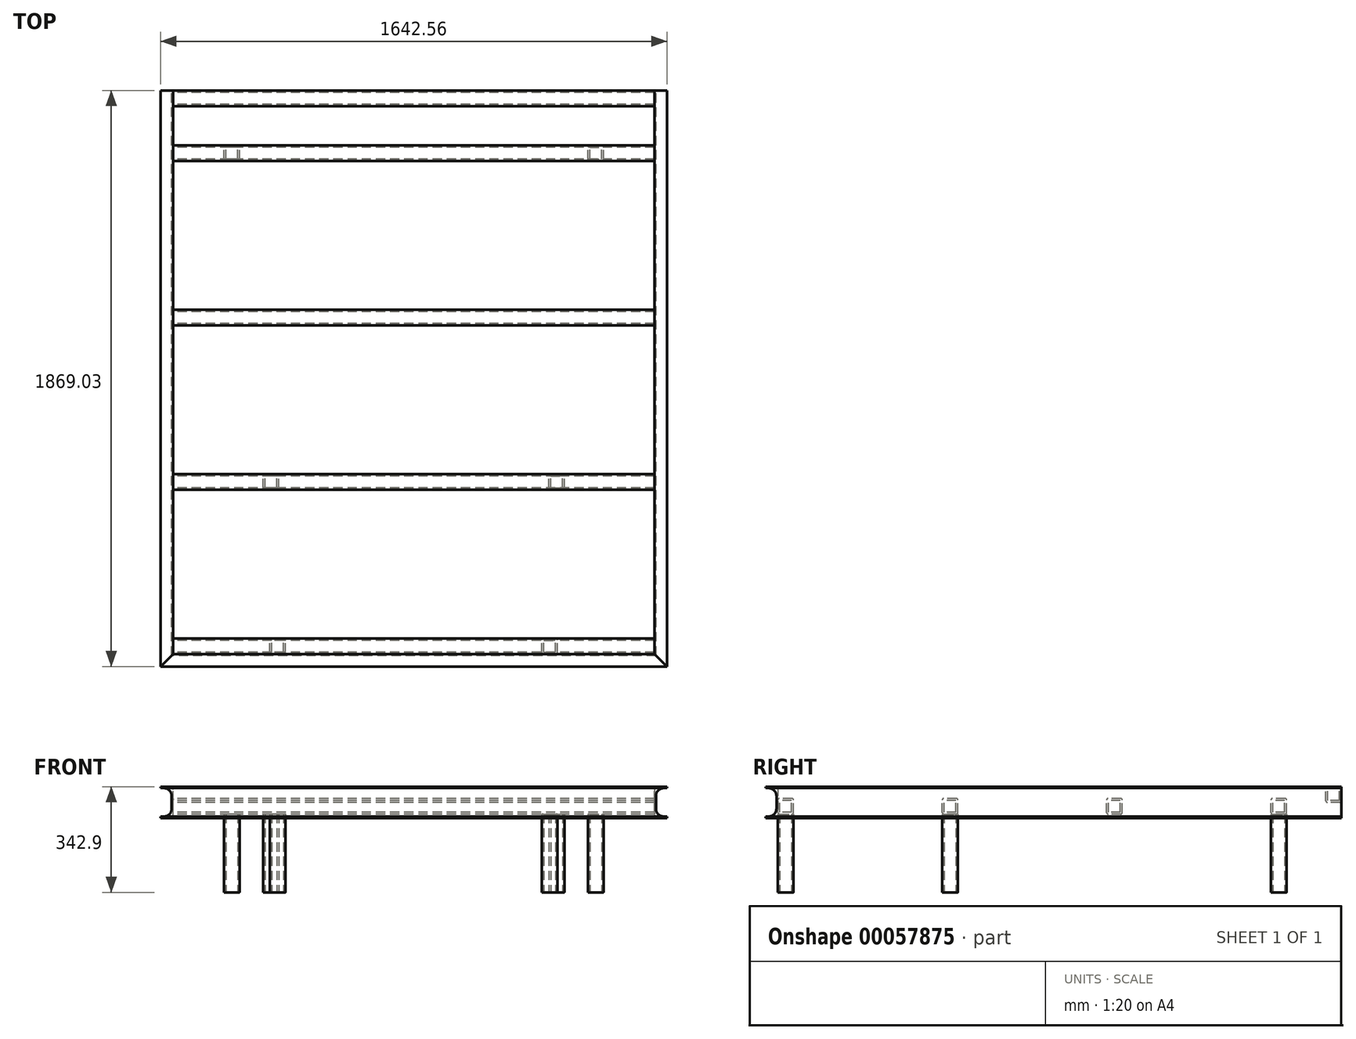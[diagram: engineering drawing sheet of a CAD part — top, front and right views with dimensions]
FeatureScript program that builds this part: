
annotation { "Feature Type Name" : "Feature", "Feature Type Description" : "" }
export const myFeature = defineFeature(function(context is Context, id is Id, definition is map)
    precondition{}
    {
        {
            var Q0;
            Q0=qCreatedBy(makeId("Top.planeOp"),FACE);
            var sketch = newSketch(context, id + "F0", { "sketchPlane" : qUnion([Q0])});
            skLineSegment(sketch, "E0.rect.bottom", {"start": v(-565.15, -25.4) * mm, "end": v(-615.95, -25.4) * mm});
            skLineSegment(sketch, "E0.rect.top", {"start": v(-565.15, 25.4) * mm, "end": v(-615.95, 25.4) * mm});
            skLineSegment(sketch, "E0.rect.left", {"start": v(-565.15, -25.4) * mm, "end": v(-565.15, 25.4) * mm});
            skLineSegment(sketch, "E0.rect.right", {"start": v(-615.95, -25.4) * mm, "end": v(-615.95, 25.4) * mm});
            skPoint(sketch, "E0.rect.middle", {"position": v(-590.55, 0) * mm});
            skLineSegment(sketch, "E1.rect.bottom", {"start": v(-571.5, -19.05) * mm, "end": v(-609.6, -19.05) * mm});
            skLineSegment(sketch, "E1.rect.top", {"start": v(-571.5, 19.05) * mm, "end": v(-609.6, 19.05) * mm});
            skLineSegment(sketch, "E1.rect.left", {"start": v(-571.5, -19.05) * mm, "end": v(-571.5, 19.05) * mm});
            skLineSegment(sketch, "E1.rect.right", {"start": v(-609.6, -19.05) * mm, "end": v(-609.6, 19.05) * mm});
            skLineSegment(sketch, "E2.rect.bottom", {"start": v(-438.15, -1092.2) * mm, "end": v(-488.95, -1092.2) * mm});
            skLineSegment(sketch, "E2.rect.top", {"start": v(-438.15, -1041.4) * mm, "end": v(-488.95, -1041.4) * mm});
            skLineSegment(sketch, "E2.rect.left", {"start": v(-438.15, -1092.2) * mm, "end": v(-438.15, -1041.4) * mm});
            skLineSegment(sketch, "E2.rect.right", {"start": v(-488.95, -1092.2) * mm, "end": v(-488.95, -1041.4) * mm});
            skPoint(sketch, "E2.rect.middle", {"position": v(-463.55, -1066.8) * mm});
            skLineSegment(sketch, "E3.rect.bottom", {"start": v(-444.5, -1085.85) * mm, "end": v(-482.6, -1085.85) * mm});
            skLineSegment(sketch, "E3.rect.top", {"start": v(-444.5, -1047.75) * mm, "end": v(-482.6, -1047.75) * mm});
            skLineSegment(sketch, "E3.rect.left", {"start": v(-444.5, -1085.85) * mm, "end": v(-444.5, -1047.75) * mm});
            skLineSegment(sketch, "E3.rect.right", {"start": v(-482.6, -1085.85) * mm, "end": v(-482.6, -1047.75) * mm});
            skLineSegment(sketch, "E4.rect.bottom", {"start": v(-415.93, -1625.6) * mm, "end": v(-466.73, -1625.6) * mm});
            skLineSegment(sketch, "E4.rect.top", {"start": v(-415.93, -1574.8) * mm, "end": v(-466.73, -1574.8) * mm});
            skLineSegment(sketch, "E4.rect.left", {"start": v(-415.93, -1625.6) * mm, "end": v(-415.93, -1574.8) * mm});
            skLineSegment(sketch, "E4.rect.right", {"start": v(-466.73, -1625.6) * mm, "end": v(-466.73, -1574.8) * mm});
            skPoint(sketch, "E4.rect.middle", {"position": v(-441.33, -1600.2) * mm});
            skLineSegment(sketch, "E5.rect.bottom", {"start": v(-422.28, -1619.25) * mm, "end": v(-460.38, -1619.25) * mm});
            skLineSegment(sketch, "E5.rect.top", {"start": v(-422.28, -1581.15) * mm, "end": v(-460.38, -1581.15) * mm});
            skLineSegment(sketch, "E5.rect.left", {"start": v(-422.28, -1619.25) * mm, "end": v(-422.28, -1581.15) * mm});
            skLineSegment(sketch, "E5.rect.right", {"start": v(-460.38, -1619.25) * mm, "end": v(-460.38, -1581.15) * mm});
            skLineSegment(sketch, "E6.MirrorCS", {"start": v(422.28, -1619.25) * mm, "end": v(460.38, -1619.25) * mm});
            skLineSegment(sketch, "E7.MirrorCS", {"start": v(565.15, -25.4) * mm, "end": v(615.95, -25.4) * mm});
            skLineSegment(sketch, "E8.MirrorCS", {"start": v(466.72, -1625.6) * mm, "end": v(466.72, -1574.8) * mm});
            skLineSegment(sketch, "E9.MirrorCS", {"start": v(422.28, -1581.15) * mm, "end": v(460.38, -1581.15) * mm});
            skLineSegment(sketch, "E10.MirrorCS", {"start": v(571.5, -19.05) * mm, "end": v(571.5, 19.05) * mm});
            skLineSegment(sketch, "E11.MirrorCS", {"start": v(571.5, 19.05) * mm, "end": v(609.6, 19.05) * mm});
            skLineSegment(sketch, "E12.MirrorCS", {"start": v(460.37, -1619.25) * mm, "end": v(460.37, -1581.15) * mm});
            skLineSegment(sketch, "E13.MirrorCS", {"start": v(571.5, -19.05) * mm, "end": v(609.6, -19.05) * mm});
            skLineSegment(sketch, "E14.MirrorCS", {"start": v(415.93, -1625.6) * mm, "end": v(466.73, -1625.6) * mm});
            skLineSegment(sketch, "E15.MirrorCS", {"start": v(565.15, -25.4) * mm, "end": v(565.15, 25.4) * mm});
            skLineSegment(sketch, "E16.MirrorCS", {"start": v(444.5, -1047.75) * mm, "end": v(482.6, -1047.75) * mm});
            skLineSegment(sketch, "E17.MirrorCS", {"start": v(422.27, -1619.25) * mm, "end": v(422.27, -1581.15) * mm});
            skLineSegment(sketch, "E18.MirrorCS", {"start": v(488.95, -1092.2) * mm, "end": v(488.95, -1041.4) * mm});
            skLineSegment(sketch, "E19.MirrorCS", {"start": v(609.6, -19.05) * mm, "end": v(609.6, 19.05) * mm});
            skLineSegment(sketch, "E20.MirrorCS", {"start": v(438.15, -1092.2) * mm, "end": v(488.95, -1092.2) * mm});
            skLineSegment(sketch, "E21.MirrorCS", {"start": v(415.93, -1574.8) * mm, "end": v(466.73, -1574.8) * mm});
            skLineSegment(sketch, "E22.MirrorCS", {"start": v(415.92, -1625.6) * mm, "end": v(415.92, -1574.8) * mm});
            skLineSegment(sketch, "E23.MirrorCS", {"start": v(482.6, -1085.85) * mm, "end": v(482.6, -1047.75) * mm});
            skLineSegment(sketch, "E24.MirrorCS", {"start": v(438.15, -1041.4) * mm, "end": v(488.95, -1041.4) * mm});
            skLineSegment(sketch, "E25.MirrorCS", {"start": v(615.95, -25.4) * mm, "end": v(615.95, 25.4) * mm});
            skLineSegment(sketch, "E26.MirrorCS", {"start": v(444.5, -1085.85) * mm, "end": v(482.6, -1085.85) * mm});
            skLineSegment(sketch, "E27.MirrorCS", {"start": v(438.15, -1092.2) * mm, "end": v(438.15, -1041.4) * mm});
            skLineSegment(sketch, "E28.MirrorCS", {"start": v(444.5, -1085.85) * mm, "end": v(444.5, -1047.75) * mm});
            skLineSegment(sketch, "E29.MirrorCS", {"start": v(565.15, 25.4) * mm, "end": v(615.95, 25.4) * mm});
            skPoint(sketch, "E30.MirrorP", {"position": v(441.33, -1600.2) * mm});
            skPoint(sketch, "E31.MirrorP", {"position": v(463.55, -1066.8) * mm});
            skPoint(sketch, "E32.MirrorP", {"position": v(590.55, 0) * mm});
            skSolve(sketch);
        }
        {
            var Q0;
            Q0 = qSketchRegion(id + "F0", true);
            extrude(context, id + "F1", {"entities" : qUnion([Q0]), "depth" : 254 * mm});
        }
        {
            var Q0;
            Q0=qCreatedBy(makeId("Right.planeOp"),FACE);
            var sketch = newSketch(context, id + "F2", { "sketchPlane" : qUnion([Q0])});
            skLineSegment(sketch, "E33.rect.bottom", {"start": v(25.4, 254) * mm, "end": v(-25.4, 254) * mm});
            skLineSegment(sketch, "E33.rect.top", {"start": v(25.4, 304.8) * mm, "end": v(-25.4, 304.8) * mm});
            skLineSegment(sketch, "E33.rect.left", {"start": v(25.4, 254) * mm, "end": v(25.4, 304.8) * mm});
            skLineSegment(sketch, "E33.rect.right", {"start": v(-25.4, 254) * mm, "end": v(-25.4, 304.8) * mm});
            skPoint(sketch, "E33.rect.middle", {"position": v(0, 279.4) * mm});
            skLineSegment(sketch, "E34.rect.bottom", {"start": v(19.05, 260.35) * mm, "end": v(-19.05, 260.35) * mm});
            skLineSegment(sketch, "E34.rect.top", {"start": v(19.05, 298.45) * mm, "end": v(-19.05, 298.45) * mm});
            skLineSegment(sketch, "E34.rect.left", {"start": v(19.05, 260.35) * mm, "end": v(19.05, 298.45) * mm});
            skLineSegment(sketch, "E34.rect.right", {"start": v(-19.05, 260.35) * mm, "end": v(-19.05, 298.45) * mm});
            skSolve(sketch);
        }
        {
            var Q0;
            Q0=makeQuery(id+"F2.imprint","IMPRINT",FACE,{"disambiguationData":[TD([[makeQuery(id+"F2.imprint","IMPRINT",EDGE,{"derivedFrom":sQuery(id+"F2.wireOp",EDGE,"E33.rect.bottom")}),-1.0]])]});
            extrude(context, id + "F3", {"entities" : qUnion([Q0]), "endBound" : BoundingType.SYMMETRIC, "depth" : 1562.1 * mm});
        }
        {
            var Q0;
            Q0=qCreatedBy(makeId("Right.planeOp"),FACE);
            var sketch = newSketch(context, id + "F4", { "sketchPlane" : qUnion([Q0])});
            skLineSegment(sketch, "E35.rect.bottom", {"start": v(-1041.4, 254) * mm, "end": v(-1092.2, 254) * mm});
            skLineSegment(sketch, "E35.rect.top", {"start": v(-1041.4, 304.8) * mm, "end": v(-1092.2, 304.8) * mm});
            skLineSegment(sketch, "E35.rect.left", {"start": v(-1041.4, 254) * mm, "end": v(-1041.4, 304.8) * mm});
            skLineSegment(sketch, "E35.rect.right", {"start": v(-1092.2, 254) * mm, "end": v(-1092.2, 304.8) * mm});
            skPoint(sketch, "E35.rect.middle", {"position": v(-1066.8, 279.4) * mm});
            skLineSegment(sketch, "E36.rect.bottom", {"start": v(-1047.75, 260.35) * mm, "end": v(-1085.85, 260.35) * mm});
            skLineSegment(sketch, "E36.rect.top", {"start": v(-1047.75, 298.45) * mm, "end": v(-1085.85, 298.45) * mm});
            skLineSegment(sketch, "E36.rect.left", {"start": v(-1047.75, 260.35) * mm, "end": v(-1047.75, 298.45) * mm});
            skLineSegment(sketch, "E36.rect.right", {"start": v(-1085.85, 260.35) * mm, "end": v(-1085.85, 298.45) * mm});
            skSolve(sketch);
        }
        {
            var Q0;
            Q0=makeQuery(id+"F4.imprint","IMPRINT",FACE,{"disambiguationData":[TD([[makeQuery(id+"F4.imprint","IMPRINT",EDGE,{"derivedFrom":sQuery(id+"F4.wireOp",EDGE,"E35.rect.bottom")}),-1.0]])]});
            extrude(context, id + "F5", {"entities" : qUnion([Q0]), "endBound" : BoundingType.SYMMETRIC, "depth" : 1562.1 * mm});
        }
        {
            var Q0;
            Q0=qCreatedBy(makeId("Right.planeOp"),FACE);
            var sketch = newSketch(context, id + "F6", { "sketchPlane" : qUnion([Q0])});
            skLineSegment(sketch, "E37.rect.bottom", {"start": v(-1574.8, 254) * mm, "end": v(-1625.6, 254) * mm});
            skLineSegment(sketch, "E37.rect.top", {"start": v(-1574.8, 304.8) * mm, "end": v(-1625.6, 304.8) * mm});
            skLineSegment(sketch, "E37.rect.left", {"start": v(-1574.8, 254) * mm, "end": v(-1574.8, 304.8) * mm});
            skLineSegment(sketch, "E37.rect.right", {"start": v(-1625.6, 254) * mm, "end": v(-1625.6, 304.8) * mm});
            skPoint(sketch, "E37.rect.middle", {"position": v(-1600.2, 279.4) * mm});
            skLineSegment(sketch, "E38.rect.bottom", {"start": v(-1581.15, 260.35) * mm, "end": v(-1619.25, 260.35) * mm});
            skLineSegment(sketch, "E38.rect.top", {"start": v(-1581.15, 298.45) * mm, "end": v(-1619.25, 298.45) * mm});
            skLineSegment(sketch, "E38.rect.left", {"start": v(-1581.15, 260.35) * mm, "end": v(-1581.15, 298.45) * mm});
            skLineSegment(sketch, "E38.rect.right", {"start": v(-1619.25, 260.35) * mm, "end": v(-1619.25, 298.45) * mm});
            skSolve(sketch);
        }
        {
            var Q0;
            Q0=makeQuery(id+"F6.imprint","IMPRINT",FACE,{"disambiguationData":[TD([[makeQuery(id+"F6.imprint","IMPRINT",EDGE,{"derivedFrom":sQuery(id+"F6.wireOp",EDGE,"E37.rect.bottom")}),-1.0]])]});
            extrude(context, id + "F7", {"entities" : qUnion([Q0]), "endBound" : BoundingType.SYMMETRIC, "depth" : 1562.1 * mm});
        }
        {
            var Q0;
            Q0=qCreatedBy(makeId("Front.planeOp"),FACE);
            var sketch = newSketch(context, id + "F8", { "sketchPlane" : qUnion([Q0])});
            skLineSegment(sketch, "E39.bottom", {"start": v(-821.28, 342.9) * mm, "end": v(-781.05, 342.9) * mm});
            skLineSegment(sketch, "E39.top", {"start": v(-821.28, 241.3) * mm, "end": v(-781.05, 241.3) * mm});
            skLineSegment(sketch, "E39.left", {"start": v(-821.28, 342.9) * mm, "end": v(-821.28, 241.3) * mm});
            skLineSegment(sketch, "E39.right", {"start": v(-781.05, 342.9) * mm, "end": v(-781.05, 241.3) * mm});
            skLineSegment(sketch, "E40.bottom", {"start": v(-821.28, 338.23) * mm, "end": v(-785.72, 338.23) * mm});
            skLineSegment(sketch, "E40.top", {"start": v(-821.28, 245.97) * mm, "end": v(-785.72, 245.97) * mm});
            skLineSegment(sketch, "E40.left", {"start": v(-821.28, 338.23) * mm, "end": v(-821.28, 245.97) * mm});
            skLineSegment(sketch, "E40.right", {"start": v(-785.72, 338.23) * mm, "end": v(-785.72, 245.97) * mm});
            skSolve(sketch);
        }
        {
            var Q0;
            {var subQ4=sQuery(id+"F8.wireOp",EDGE,"E39.bottom");Q0=makeQuery(id+"F8.imprint","IMPRINT",FACE,{"disambiguationData":[TD([[makeQuery(id+"F8.imprint","IMPRINT",EDGE,{"derivedFrom":subQ4}),-1.0]])]});}
            extrude(context, id + "F9", {"entities" : qUnion([Q0]), "depth" : 1665.83 * mm, "hasSecondDirection" : true, "secondDirectionOppositeDirection" : true, "secondDirectionDepth" : 203.2 * mm});
        }
        {
            var Q0;
            Q0=makeQuery(id+"F9.opExtrude","SWEPT_EDGE",EDGE,{"disambiguationData":[OSD([sQuery(id+"F8.wireOp",EDGE,"E40.bottom"),sQuery(id+"F8.wireOp",EDGE,"E40.right")])]});
            var Q1;
            Q1=makeQuery(id+"F9.opExtrude","SWEPT_EDGE",EDGE,{"disambiguationData":[OSD([sQuery(id+"F8.wireOp",EDGE,"E40.top"),sQuery(id+"F8.wireOp",EDGE,"E40.right")])]});
            fillet(context, id + "F10", {"entities" : qUnion([Q0, Q1]), "radius" : 25.4 * mm, "tangentPropagation" : true, "allowEdgeOverflow" : false});
        }
        {
            var Q0;
            Q0=makeQuery(id+"F9.opExtrude","SWEPT_BODY",BODY,{"disambiguationData":[OSD([sQuery(id+"F8.wireOp",EDGE,"E39.bottom"),sQuery(id+"F8.wireOp",EDGE,"E39.top"),sQuery(id+"F8.wireOp",EDGE,"E39.left"),sQuery(id+"F8.wireOp",EDGE,"E39.right"),sQuery(id+"F8.wireOp",EDGE,"E40.bottom"),sQuery(id+"F8.wireOp",EDGE,"E40.top"),sQuery(id+"F8.wireOp",EDGE,"E40.right")])]});
            var Q1;
            Q1=qCreatedBy(makeId("Right.planeOp"),FACE);
            mirror(context, id + "F11", {"entities" : qUnion([Q0]), "mirrorPlane" : qUnion([Q1])});
        }
        {
            var Q0;
            Q0=makeQuery(id+"F7.opExtrude","SWEPT_EDGE",EDGE,{"disambiguationData":[OSD([sQuery(id+"F6.wireOp",EDGE,"E37.rect.top"),sQuery(id+"F6.wireOp",EDGE,"E37.rect.right")])]});
            var Q1;
            Q1=makeQuery(id+"F7.opExtrude","SWEPT_EDGE",EDGE,{"disambiguationData":[OSD([sQuery(id+"F6.wireOp",EDGE,"E37.rect.bottom"),sQuery(id+"F6.wireOp",EDGE,"E37.rect.right")])]});
            var Q2;
            Q2=makeQuery(id+"F7.opExtrude","SWEPT_EDGE",EDGE,{"disambiguationData":[OSD([sQuery(id+"F6.wireOp",EDGE,"E37.rect.top"),sQuery(id+"F6.wireOp",EDGE,"E37.rect.left")])]});
            var Q3;
            Q3=makeQuery(id+"F7.opExtrude","SWEPT_EDGE",EDGE,{"disambiguationData":[OSD([sQuery(id+"F6.wireOp",EDGE,"E37.rect.bottom"),sQuery(id+"F6.wireOp",EDGE,"E37.rect.left")])]});
            var Q4;
            Q4=makeQuery(id+"F1.opExtrude","SWEPT_EDGE",EDGE,{"disambiguationData":[OSD([sQuery(id+"F0.wireOp",EDGE,"E4.rect.bottom"),sQuery(id+"F0.wireOp",EDGE,"E4.rect.left")])]});
            var Q5;
            Q5=makeQuery(id+"F1.opExtrude","SWEPT_EDGE",EDGE,{"disambiguationData":[OSD([sQuery(id+"F0.wireOp",EDGE,"E4.rect.bottom"),sQuery(id+"F0.wireOp",EDGE,"E4.rect.right")])]});
            var Q6;
            Q6=makeQuery(id+"F1.opExtrude","SWEPT_EDGE",EDGE,{"disambiguationData":[OSD([sQuery(id+"F0.wireOp",EDGE,"E14.MirrorCS"),sQuery(id+"F0.wireOp",EDGE,"E22.MirrorCS")])]});
            var Q7;
            Q7=makeQuery(id+"F1.opExtrude","SWEPT_EDGE",EDGE,{"disambiguationData":[OSD([sQuery(id+"F0.wireOp",EDGE,"E8.MirrorCS"),sQuery(id+"F0.wireOp",EDGE,"E14.MirrorCS")])]});
            var Q8;
            Q8=makeQuery(id+"F1.opExtrude","SWEPT_EDGE",EDGE,{"disambiguationData":[OSD([sQuery(id+"F0.wireOp",EDGE,"E4.rect.top"),sQuery(id+"F0.wireOp",EDGE,"E4.rect.right")])]});
            var Q9;
            Q9=makeQuery(id+"F1.opExtrude","SWEPT_EDGE",EDGE,{"disambiguationData":[OSD([sQuery(id+"F0.wireOp",EDGE,"E21.MirrorCS"),sQuery(id+"F0.wireOp",EDGE,"E22.MirrorCS")])]});
            var Q10;
            Q10=makeQuery(id+"F1.opExtrude","SWEPT_EDGE",EDGE,{"disambiguationData":[OSD([sQuery(id+"F0.wireOp",EDGE,"E4.rect.top"),sQuery(id+"F0.wireOp",EDGE,"E4.rect.left")])]});
            var Q11;
            Q11=makeQuery(id+"F1.opExtrude","SWEPT_EDGE",EDGE,{"disambiguationData":[OSD([sQuery(id+"F0.wireOp",EDGE,"E8.MirrorCS"),sQuery(id+"F0.wireOp",EDGE,"E21.MirrorCS")])]});
            var Q12;
            Q12=makeQuery(id+"F5.opExtrude","SWEPT_EDGE",EDGE,{"disambiguationData":[OSD([sQuery(id+"F4.wireOp",EDGE,"E35.rect.bottom"),sQuery(id+"F4.wireOp",EDGE,"E35.rect.right")])]});
            var Q13;
            Q13=makeQuery(id+"F5.opExtrude","SWEPT_EDGE",EDGE,{"disambiguationData":[OSD([sQuery(id+"F4.wireOp",EDGE,"E35.rect.bottom"),sQuery(id+"F4.wireOp",EDGE,"E35.rect.left")])]});
            var Q14;
            Q14=makeQuery(id+"F5.opExtrude","SWEPT_EDGE",EDGE,{"disambiguationData":[OSD([sQuery(id+"F4.wireOp",EDGE,"E35.rect.top"),sQuery(id+"F4.wireOp",EDGE,"E35.rect.left")])]});
            var Q15;
            Q15=makeQuery(id+"F5.opExtrude","SWEPT_EDGE",EDGE,{"disambiguationData":[OSD([sQuery(id+"F4.wireOp",EDGE,"E35.rect.top"),sQuery(id+"F4.wireOp",EDGE,"E35.rect.right")])]});
            var Q16;
            Q16=makeQuery(id+"F1.opExtrude","SWEPT_EDGE",EDGE,{"disambiguationData":[OSD([sQuery(id+"F0.wireOp",EDGE,"E18.MirrorCS"),sQuery(id+"F0.wireOp",EDGE,"E20.MirrorCS")])]});
            var Q17;
            Q17=makeQuery(id+"F1.opExtrude","SWEPT_EDGE",EDGE,{"disambiguationData":[OSD([sQuery(id+"F0.wireOp",EDGE,"E20.MirrorCS"),sQuery(id+"F0.wireOp",EDGE,"E27.MirrorCS")])]});
            var Q18;
            Q18=makeQuery(id+"F1.opExtrude","SWEPT_EDGE",EDGE,{"disambiguationData":[OSD([sQuery(id+"F0.wireOp",EDGE,"E18.MirrorCS"),sQuery(id+"F0.wireOp",EDGE,"E24.MirrorCS")])]});
            var Q19;
            Q19=makeQuery(id+"F1.opExtrude","SWEPT_EDGE",EDGE,{"disambiguationData":[OSD([sQuery(id+"F0.wireOp",EDGE,"E2.rect.top"),sQuery(id+"F0.wireOp",EDGE,"E2.rect.left")])]});
            var Q20;
            Q20=makeQuery(id+"F1.opExtrude","SWEPT_EDGE",EDGE,{"disambiguationData":[OSD([sQuery(id+"F0.wireOp",EDGE,"E2.rect.bottom"),sQuery(id+"F0.wireOp",EDGE,"E2.rect.left")])]});
            var Q21;
            Q21=makeQuery(id+"F1.opExtrude","SWEPT_EDGE",EDGE,{"disambiguationData":[OSD([sQuery(id+"F0.wireOp",EDGE,"E2.rect.bottom"),sQuery(id+"F0.wireOp",EDGE,"E2.rect.right")])]});
            var Q22;
            Q22=makeQuery(id+"F1.opExtrude","SWEPT_EDGE",EDGE,{"disambiguationData":[OSD([sQuery(id+"F0.wireOp",EDGE,"E24.MirrorCS"),sQuery(id+"F0.wireOp",EDGE,"E27.MirrorCS")])]});
            var Q23;
            Q23=makeQuery(id+"F1.opExtrude","SWEPT_EDGE",EDGE,{"disambiguationData":[OSD([sQuery(id+"F0.wireOp",EDGE,"E2.rect.top"),sQuery(id+"F0.wireOp",EDGE,"E2.rect.right")])]});
            var Q24;
            Q24=makeQuery(id+"F1.opExtrude","SWEPT_EDGE",EDGE,{"disambiguationData":[OSD([sQuery(id+"F0.wireOp",EDGE,"E0.rect.top"),sQuery(id+"F0.wireOp",EDGE,"E0.rect.right")])]});
            var Q25;
            Q25=makeQuery(id+"F1.opExtrude","SWEPT_EDGE",EDGE,{"disambiguationData":[OSD([sQuery(id+"F0.wireOp",EDGE,"E0.rect.bottom"),sQuery(id+"F0.wireOp",EDGE,"E0.rect.right")])]});
            var Q26;
            Q26=makeQuery(id+"F1.opExtrude","SWEPT_EDGE",EDGE,{"disambiguationData":[OSD([sQuery(id+"F0.wireOp",EDGE,"E0.rect.top"),sQuery(id+"F0.wireOp",EDGE,"E0.rect.left")])]});
            var Q27;
            Q27=makeQuery(id+"F3.opExtrude","SWEPT_EDGE",EDGE,{"disambiguationData":[OSD([sQuery(id+"F2.wireOp",EDGE,"E33.rect.bottom"),sQuery(id+"F2.wireOp",EDGE,"E33.rect.right")])]});
            var Q28;
            Q28=makeQuery(id+"F3.opExtrude","SWEPT_EDGE",EDGE,{"disambiguationData":[OSD([sQuery(id+"F2.wireOp",EDGE,"E33.rect.bottom"),sQuery(id+"F2.wireOp",EDGE,"E33.rect.left")])]});
            var Q29;
            Q29=makeQuery(id+"F3.opExtrude","SWEPT_EDGE",EDGE,{"disambiguationData":[OSD([sQuery(id+"F2.wireOp",EDGE,"E33.rect.top"),sQuery(id+"F2.wireOp",EDGE,"E33.rect.left")])]});
            var Q30;
            Q30=makeQuery(id+"F1.opExtrude","SWEPT_EDGE",EDGE,{"disambiguationData":[OSD([sQuery(id+"F0.wireOp",EDGE,"E25.MirrorCS"),sQuery(id+"F0.wireOp",EDGE,"E29.MirrorCS")])]});
            var Q31;
            Q31=makeQuery(id+"F1.opExtrude","SWEPT_EDGE",EDGE,{"disambiguationData":[OSD([sQuery(id+"F0.wireOp",EDGE,"E15.MirrorCS"),sQuery(id+"F0.wireOp",EDGE,"E29.MirrorCS")])]});
            var Q32;
            Q32=makeQuery(id+"F1.opExtrude","SWEPT_EDGE",EDGE,{"disambiguationData":[OSD([sQuery(id+"F0.wireOp",EDGE,"E7.MirrorCS"),sQuery(id+"F0.wireOp",EDGE,"E15.MirrorCS")])]});
            var Q33;
            Q33=makeQuery(id+"F3.opExtrude","SWEPT_EDGE",EDGE,{"disambiguationData":[OSD([sQuery(id+"F2.wireOp",EDGE,"E33.rect.top"),sQuery(id+"F2.wireOp",EDGE,"E33.rect.right")])]});
            var Q34;
            Q34=makeQuery(id+"F1.opExtrude","SWEPT_EDGE",EDGE,{"disambiguationData":[OSD([sQuery(id+"F0.wireOp",EDGE,"E0.rect.bottom"),sQuery(id+"F0.wireOp",EDGE,"E0.rect.left")])]});
            var Q35;
            Q35=makeQuery(id+"F1.opExtrude","SWEPT_EDGE",EDGE,{"disambiguationData":[OSD([sQuery(id+"F0.wireOp",EDGE,"E7.MirrorCS"),sQuery(id+"F0.wireOp",EDGE,"E25.MirrorCS")])]});
            fillet(context, id + "F12", {"entities" : qUnion([Q0, Q1, Q2, Q3, Q4, Q5, Q6, Q7, Q8, Q9, Q10, Q11, Q12, Q13, Q14, Q15, Q16, Q17, Q18, Q19, Q20, Q21, Q22, Q23, Q24, Q25, Q26, Q27, Q28, Q29, Q30, Q31, Q32, Q33, Q34, Q35]), "radius" : 5.08 * mm, "tangentPropagation" : true, "allowEdgeOverflow" : false});
        }
        {
            var Q0;
            Q0=qCreatedBy(makeId("Right.planeOp"),FACE);
            var sketch = newSketch(context, id + "F13", { "sketchPlane" : qUnion([Q0])});
            skLineSegment(sketch, "E41.bottom", {"start": v(-1665.83, 342.9) * mm, "end": v(-1625.6, 342.9) * mm});
            skLineSegment(sketch, "E41.top", {"start": v(-1665.83, 241.3) * mm, "end": v(-1625.6, 241.3) * mm});
            skLineSegment(sketch, "E41.left", {"start": v(-1665.83, 342.9) * mm, "end": v(-1665.83, 241.3) * mm});
            skLineSegment(sketch, "E41.right", {"start": v(-1625.6, 342.9) * mm, "end": v(-1625.6, 241.3) * mm});
            skLineSegment(sketch, "E42.bottom", {"start": v(-1665.83, 338.23) * mm, "end": v(-1630.27, 338.23) * mm});
            skLineSegment(sketch, "E42.top", {"start": v(-1665.83, 245.97) * mm, "end": v(-1630.27, 245.97) * mm});
            skLineSegment(sketch, "E42.left", {"start": v(-1665.83, 338.23) * mm, "end": v(-1665.83, 245.97) * mm});
            skLineSegment(sketch, "E42.right", {"start": v(-1630.27, 338.23) * mm, "end": v(-1630.27, 245.97) * mm});
            skSolve(sketch);
        }
        {
            var Q0;
            {var subQ4=sQuery(id+"F13.wireOp",EDGE,"E41.bottom");Q0=makeQuery(id+"F13.imprint","IMPRINT",FACE,{"disambiguationData":[TD([[makeQuery(id+"F13.imprint","IMPRINT",EDGE,{"derivedFrom":subQ4}),-1.0]])]});}
            var Q1;
            Q1=sQuery(id+"F13.wireOp",EDGE,"E41.bottom");
            var Q2;
            Q2=sQuery(id+"F13.wireOp",EDGE,"E41.top");
            var Q3;
            Q3=sQuery(id+"F13.wireOp",EDGE,"E41.left");
            var Q4;
            Q4=sQuery(id+"F13.wireOp",EDGE,"E42.bottom");
            var Q5;
            Q5=sQuery(id+"F13.wireOp",EDGE,"E42.top");
            var Q6;
            Q6=sQuery(id+"F13.wireOp",EDGE,"E42.right");
            var Q7;
            Q7=sQuery(id+"F13.wireOp",EDGE,"E41.right");
            extrude(context, id + "F14", {"entities" : qUnion([Q0]), "surfaceEntities" : qUnion([Q1, Q2, Q3, Q4, Q5, Q6, Q7]), "endBound" : BoundingType.SYMMETRIC, "depth" : 1642.57 * mm});
        }
        {
            var Q0;
            Q0=makeQuery(id+"F14.opExtrude","SWEPT_EDGE",EDGE,{"disambiguationData":[OSD([sQuery(id+"F13.wireOp",EDGE,"E42.top"),sQuery(id+"F13.wireOp",EDGE,"E42.right")])]});
            var Q1;
            Q1=makeQuery(id+"F14.opExtrude","SWEPT_EDGE",EDGE,{"disambiguationData":[OSD([sQuery(id+"F13.wireOp",EDGE,"E42.bottom"),sQuery(id+"F13.wireOp",EDGE,"E42.right")])]});
            fillet(context, id + "F15", {"entities" : qUnion([Q0, Q1]), "radius" : 25.4 * mm, "tangentPropagation" : true, "allowEdgeOverflow" : false});
        }
        {
            var Q0;
            Q0=makeQuery(id+"F14.opExtrude","CAP_EDGE",EDGE,{"disambiguationData":[OSD([sQuery(id+"F13.wireOp",EDGE,"E41.right")])],"isStart":true});
            chamfer(context, id + "F16", {"entities" : qUnion([Q0]), "width" : 40.23 * mm, "tangentPropagation" : true});
        }
        {
            var Q0;
            Q0=makeQuery(id+"F9.opExtrude","CAP_EDGE",EDGE,{"disambiguationData":[OSD([sQuery(id+"F8.wireOp",EDGE,"E39.right")])],"isStart":false});
            chamfer(context, id + "F17", {"entities" : qUnion([Q0]), "width" : 40.23 * mm, "tangentPropagation" : true});
        }
        {
            var Q0;
            Q0=makeQuery(id+"F11.opPattern","COPY",EDGE,{"derivedFrom":makeQuery(id+"F9.opExtrude","CAP_EDGE",EDGE,{"disambiguationData":[OSD([sQuery(id+"F8.wireOp",EDGE,"E39.right")])],"isStart":false}),"instanceName":"1"});
            var Q1;
            Q1=makeQuery(id+"F14.opExtrude","CAP_EDGE",EDGE,{"disambiguationData":[OSD([sQuery(id+"F13.wireOp",EDGE,"E41.right")])],"isStart":false});
            chamfer(context, id + "F18", {"entities" : qUnion([Q0, Q1]), "width" : 40.23 * mm, "tangentPropagation" : true});
        }
        {
            var Q0;
            Q0=qCreatedBy(makeId("Right.planeOp"),FACE);
            var sketch = newSketch(context, id + "F19", { "sketchPlane" : qUnion([Q0])});
            skLineSegment(sketch, "E43.rect.bottom", {"start": v(203.2, 292.1) * mm, "end": v(152.4, 292.1) * mm});
            skLineSegment(sketch, "E43.rect.top", {"start": v(203.2, 342.9) * mm, "end": v(152.4, 342.9) * mm});
            skLineSegment(sketch, "E43.rect.left", {"start": v(203.2, 292.1) * mm, "end": v(203.2, 342.9) * mm});
            skLineSegment(sketch, "E43.rect.right", {"start": v(152.4, 292.1) * mm, "end": v(152.4, 342.9) * mm});
            skPoint(sketch, "E43.rect.middle", {"position": v(177.8, 317.5) * mm});
            skLineSegment(sketch, "E44.rect.bottom", {"start": v(196.85, 298.45) * mm, "end": v(158.75, 298.45) * mm});
            skLineSegment(sketch, "E44.rect.top", {"start": v(196.85, 336.55) * mm, "end": v(158.75, 336.55) * mm});
            skLineSegment(sketch, "E44.rect.left", {"start": v(196.85, 298.45) * mm, "end": v(196.85, 336.55) * mm});
            skLineSegment(sketch, "E44.rect.right", {"start": v(158.75, 298.45) * mm, "end": v(158.75, 336.55) * mm});
            skSolve(sketch);
        }
        {
            var Q0;
            Q0 = qSketchRegion(id + "F19", true);
            extrude(context, id + "F20", {"entities" : qUnion([Q0]), "endBound" : BoundingType.SYMMETRIC, "depth" : 1562.1 * mm});
        }
        {
            var Q0;
            Q0=makeQuery(id+"F20.opExtrude","SWEPT_EDGE",EDGE,{"disambiguationData":[OSD([sQuery(id+"F19.wireOp",EDGE,"E43.rect.top"),sQuery(id+"F19.wireOp",EDGE,"E43.rect.right")])]});
            var Q1;
            Q1=makeQuery(id+"F20.opExtrude","SWEPT_EDGE",EDGE,{"disambiguationData":[OSD([sQuery(id+"F19.wireOp",EDGE,"E43.rect.bottom"),sQuery(id+"F19.wireOp",EDGE,"E43.rect.right")])]});
            var Q2;
            Q2=makeQuery(id+"F20.opExtrude","SWEPT_EDGE",EDGE,{"disambiguationData":[OSD([sQuery(id+"F19.wireOp",EDGE,"E43.rect.top"),sQuery(id+"F19.wireOp",EDGE,"E43.rect.left")])]});
            var Q3;
            Q3=makeQuery(id+"F20.opExtrude","SWEPT_EDGE",EDGE,{"disambiguationData":[OSD([sQuery(id+"F19.wireOp",EDGE,"E43.rect.bottom"),sQuery(id+"F19.wireOp",EDGE,"E43.rect.left")])]});
            fillet(context, id + "F21", {"entities" : qUnion([Q0, Q1, Q2, Q3]), "radius" : 5.08 * mm, "tangentPropagation" : true, "allowEdgeOverflow" : false});
        }
        {
            var Q0;
            Q0=qCreatedBy(makeId("Right.planeOp"),FACE);
            var sketch = newSketch(context, id + "F22", { "sketchPlane" : qUnion([Q0])});
            skLineSegment(sketch, "E45.rect.bottom", {"start": v(-508, 254) * mm, "end": v(-558.8, 254) * mm});
            skLineSegment(sketch, "E45.rect.top", {"start": v(-508, 304.8) * mm, "end": v(-558.8, 304.8) * mm});
            skLineSegment(sketch, "E45.rect.left", {"start": v(-508, 254) * mm, "end": v(-508, 304.8) * mm});
            skLineSegment(sketch, "E45.rect.right", {"start": v(-558.8, 254) * mm, "end": v(-558.8, 304.8) * mm});
            skPoint(sketch, "E45.rect.middle", {"position": v(-533.4, 279.4) * mm});
            skLineSegment(sketch, "E46.rect.bottom", {"start": v(-514.35, 260.35) * mm, "end": v(-552.45, 260.35) * mm});
            skLineSegment(sketch, "E46.rect.top", {"start": v(-514.35, 298.45) * mm, "end": v(-552.45, 298.45) * mm});
            skLineSegment(sketch, "E46.rect.left", {"start": v(-514.35, 260.35) * mm, "end": v(-514.35, 298.45) * mm});
            skLineSegment(sketch, "E46.rect.right", {"start": v(-552.45, 260.35) * mm, "end": v(-552.45, 298.45) * mm});
            skSolve(sketch);
        }
        {
            var Q0;
            Q0 = qSketchRegion(id + "F22", true);
            extrude(context, id + "F23", {"entities" : qUnion([Q0]), "endBound" : BoundingType.SYMMETRIC, "depth" : 1562.1 * mm});
        }
        {
            var Q0;
            Q0=makeQuery(id+"F23.opExtrude","SWEPT_EDGE",EDGE,{"disambiguationData":[OSD([sQuery(id+"F22.wireOp",EDGE,"E45.rect.top"),sQuery(id+"F22.wireOp",EDGE,"E45.rect.left")])]});
            var Q1;
            Q1=makeQuery(id+"F23.opExtrude","SWEPT_EDGE",EDGE,{"disambiguationData":[OSD([sQuery(id+"F22.wireOp",EDGE,"E45.rect.bottom"),sQuery(id+"F22.wireOp",EDGE,"E45.rect.left")])]});
            var Q2;
            Q2=makeQuery(id+"F23.opExtrude","SWEPT_EDGE",EDGE,{"disambiguationData":[OSD([sQuery(id+"F22.wireOp",EDGE,"E45.rect.top"),sQuery(id+"F22.wireOp",EDGE,"E45.rect.right")])]});
            var Q3;
            Q3=makeQuery(id+"F23.opExtrude","SWEPT_EDGE",EDGE,{"disambiguationData":[OSD([sQuery(id+"F22.wireOp",EDGE,"E45.rect.bottom"),sQuery(id+"F22.wireOp",EDGE,"E45.rect.right")])]});
            fillet(context, id + "F24", {"entities" : qUnion([Q0, Q1, Q2, Q3]), "radius" : 5.08 * mm, "tangentPropagation" : true, "allowEdgeOverflow" : false});
        }
    });
